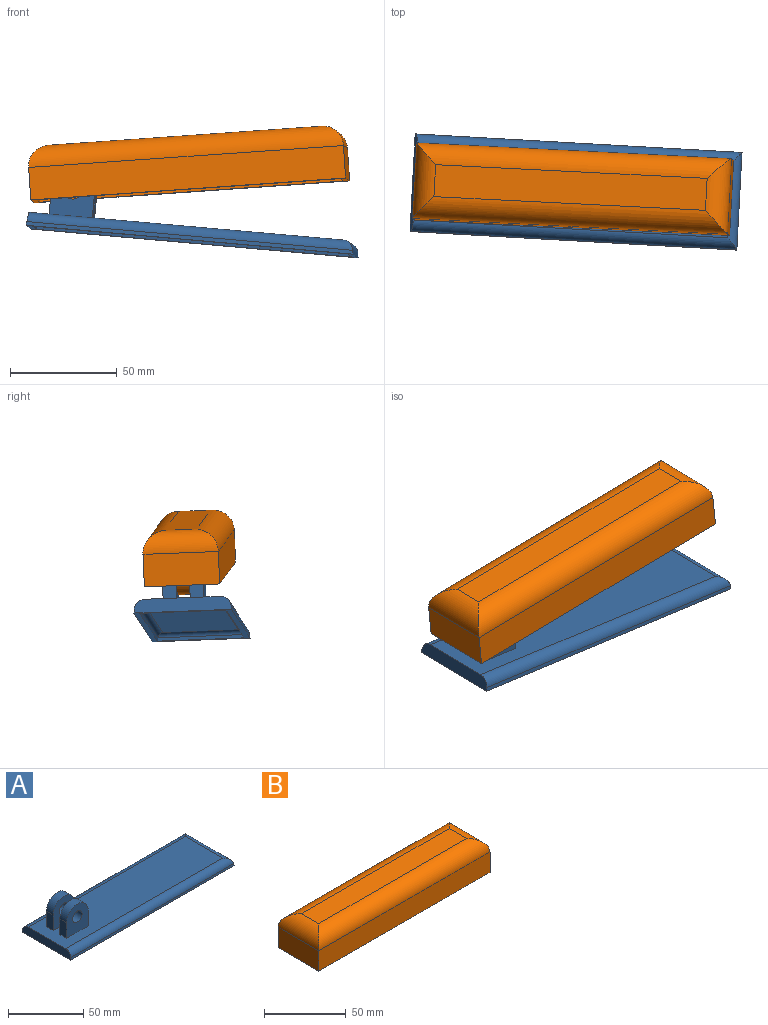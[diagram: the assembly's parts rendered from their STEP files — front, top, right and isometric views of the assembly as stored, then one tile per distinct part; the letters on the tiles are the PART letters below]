
ASSEMBLY  parts=2 mates=1
PART A: 41 faces, bbox 153.7x45.8x29.2 mm
  f0: plane 12.7x6.35mm, normal (1,0,0), area 80.6mm2, adj f1,f4,f5,f6
  f1: cylinder r=10.16mm len=20.32mm, axis (0,-1,0), area 202.7mm2, adj f0,f3,f4,f5
  f2: cylinder r=4.45mm len=8.89mm, axis (0,-1,0), area 177.3mm2, adj f4,f5
  f3: plane 12.7x6.35mm, normal (-1,0,0), area 80.6mm2, adj f1,f4,f5,f6
  f4: plane 22.86x20.32mm, normal (0,-1,0), area 358.1mm2, adj f0,f1,f2,f3,f6
  f5: plane 22.86x20.32mm, normal (0,1,0), area 358.1mm2, adj f0,f1,f2,f3,f6
  f6: plane 147.83x35.3mm, normal (0,0,1), area 4960.5mm2, adj f0,f3,f4,f5,f7,f10,f11,f12
  f7: plane 12.7x6.35mm, normal (1,0,0), area 80.6mm2, adj f6,f8,f11,f12
  f8: cylinder r=10.16mm len=20.32mm, axis (0,-1,0), area 202.7mm2, adj f7,f10,f11,f12
  f9: cylinder r=4.45mm len=8.89mm, axis (0,-1,0), area 177.3mm2, adj f11,f12
  f10: plane 12.7x6.35mm, normal (-1,0,0), area 80.6mm2, adj f6,f8,f11,f12
  f11: plane 22.86x20.32mm, normal (0,-1,0), area 358.1mm2, adj f6,f7,f8,f9,f10
  f12: plane 22.86x20.32mm, normal (0,1,0), area 358.1mm2, adj f6,f7,f8,f9,f10
  f13: plane 45.79x1.8mm, normal (0.99,0,0.1), area 82.6mm2, adj f14,f16,f17,f19
  f14: plane 153.74x1.8mm, normal (0,0.99,0.1), area 278.1mm2, adj f13,f15,f17,f20
  f15: plane 45.79x6.35mm, normal (-0.99,0,0.1), area 279.4mm2, adj f6,f14,f16,f17,f18,f20
  f16: plane 153.74x1.8mm, normal (0,-0.99,0.1), area 278.1mm2, adj f13,f15,f17,f18
  f17: plane 153.74x45.79mm, normal (0,0,-1), area 993.1mm2, adj f13,f14,f15,f16,f34,f35,f36,f37
  f18: cylinder r=5.08mm len=153.36mm, axis (1,0,0), area 1125.3mm2, adj f6,f15,f16,f19
  f19: cylinder r=5.08mm len=45.41mm, axis (0,-1,0), area 309.1mm2, adj f6,f13,f18,f20
  f20: cylinder r=5.08mm len=153.36mm, axis (1,0,0), area 1125.3mm2, adj f6,f14,f15,f19
  f21: plane 15.24x1.27mm, normal (-1,0,0), area 19.4mm2, adj f22,f25,f26,f27
  f22: cylinder r=7.62mm len=15.24mm, axis (0,-1,0), area 30.4mm2, adj f21,f24,f25,f26
  f23: cylinder r=6.99mm len=13.97mm, axis (0,-1,0), area 55.7mm2, adj f25,f26
  f24: plane 15.24x1.27mm, normal (1,0,0), area 19.4mm2, adj f22,f25,f26,f27
  f25: plane 22.86x15.24mm, normal (0,1,0), area 170.2mm2, adj f21,f22,f23,f24,f27
  f26: plane 22.86x15.24mm, normal (0,-1,0), area 170.2mm2, adj f21,f22,f23,f24,f27
  f27: plane 145.54x35.3mm, normal (0,0,-1), area 5099.1mm2, adj f21,f24,f25,f26,f28,f31,f32,f33
  f28: plane 15.24x1.27mm, normal (-1,0,0), area 19.4mm2, adj f27,f29,f32,f33
  f29: cylinder r=7.62mm len=15.24mm, axis (0,-1,0), area 30.4mm2, adj f28,f31,f32,f33
  f30: cylinder r=6.99mm len=13.97mm, axis (0,-1,0), area 55.7mm2, adj f32,f33
  f31: plane 15.24x1.27mm, normal (1,0,0), area 19.4mm2, adj f27,f29,f32,f33
  f32: plane 22.86x15.24mm, normal (0,1,0), area 170.2mm2, adj f27,f28,f29,f30,f31
  f33: plane 22.86x15.24mm, normal (0,-1,0), area 170.2mm2, adj f27,f28,f29,f30,f31
  f34: plane 40.68x1.54mm, normal (-0.99,0,-0.1), area 62.6mm2, adj f17,f35,f37,f39
  f35: plane 148.63x1.54mm, normal (0,-0.99,-0.1), area 229.2mm2, adj f17,f34,f36,f40
  f36: plane 40.68x3.81mm, normal (0.99,0,-0.1), area 152.1mm2, adj f17,f27,f35,f37,f38,f40
  f37: plane 148.63x1.54mm, normal (0,0.99,-0.1), area 229.2mm2, adj f17,f34,f36,f38
  f38: cylinder r=2.54mm len=148.3mm, axis (1,0,0), area 548.1mm2, adj f27,f36,f37,f39
  f39: cylinder r=2.54mm len=40.35mm, axis (0,-1,0), area 143mm2, adj f27,f34,f38,f40
  f40: cylinder r=2.54mm len=148.3mm, axis (1,0,0), area 548.1mm2, adj f27,f35,f36,f39
PART B: 25 faces, bbox 147.8x35.3x31.1 mm
  f0: plane 28.58x19.05mm, normal (0,1,0), area 443.3mm2, adj f16,f21,f22,f23,f24
  f1: plane 28.58x19.05mm, normal (0,-1,0), area 443.3mm2, adj f16,f21,f22,f23,f24
  f2: plane 35.3x15.24mm, normal (1,0,0), area 538mm2, adj f3,f5,f7,f10
  f3: plane 147.83x15.24mm, normal (0,1,0), area 2252.9mm2, adj f2,f4,f7,f11
  f4: plane 35.3x15.24mm, normal (-1,0,0), area 538mm2, adj f3,f5,f7,f9
  f5: plane 147.83x15.24mm, normal (0,-1,0), area 2252.9mm2, adj f2,f4,f7,f8
  f6: plane 127.51x14.98mm, normal (0,0,1), area 1910.3mm2, adj f8,f9,f10,f11
  f7: plane 147.83x35.3mm, normal (0,0,-1), area 904.5mm2, adj f2,f3,f4,f5,f12,f13,f14,f15
  f8: cylinder r=10.16mm len=147.83mm, axis (1,0,0), area 2241.4mm2, adj f5,f6,f9,f10
  f9: cylinder r=10.16mm len=35.3mm, axis (0,-1,0), area 445.6mm2, adj f4,f6,f8,f11
  f10: cylinder r=10.16mm len=35.3mm, axis (0,1,0), area 445.6mm2, adj f2,f6,f8,f11
  f11: cylinder r=10.16mm len=147.83mm, axis (-1,0,0), area 2241.4mm2, adj f3,f6,f9,f10
  f12: plane 30.22x15.24mm, normal (-1,0,0), area 460.6mm2, adj f7,f13,f15,f19
  f13: plane 142.75x15.24mm, normal (0,-1,0), area 2175.4mm2, adj f7,f12,f14,f20
  f14: plane 30.22x15.24mm, normal (1,0,0), area 460.6mm2, adj f7,f13,f15,f18
  f15: plane 142.75x15.24mm, normal (0,1,0), area 2175.4mm2, adj f7,f12,f14,f17
  f16: plane 127.51x14.98mm, normal (0,0,-1), area 1789.3mm2, adj f0,f1,f17,f18,f19,f20,f22
  f17: cylinder r=7.62mm len=142.75mm, axis (1,0,0), area 1642.3mm2, adj f15,f16,f18,f19
  f18: cylinder r=7.62mm len=30.22mm, axis (0,-1,0), area 295.5mm2, adj f14,f16,f17,f20,f21
  f19: cylinder r=7.62mm len=30.22mm, axis (0,1,0), area 295.5mm2, adj f12,f16,f17,f20
  f20: cylinder r=7.62mm len=142.75mm, axis (-1,0,0), area 1642.3mm2, adj f13,f16,f18,f19
  f21: plane 19.05x6.35mm, normal (-1,0,0), area 121mm2, adj f0,f1,f18,f24
  f22: plane 19.05x6.35mm, normal (1,0,0), area 121mm2, adj f0,f1,f16,f24
  f23: cylinder r=4.45mm len=8.89mm, axis (0,1,0), area 177.3mm2, adj f0,f1
  f24: cylinder r=9.53mm len=19.05mm, axis (0,1,0), area 190mm2, adj f0,f1,f21,f22
PLACE A rot(axis=(-0.33,0.81,-0.5),6.3deg) t=(-76.16,48.75,83.4)mm fixed
PLACE B rot(axis=(-0.42,-0.72,-0.55),5.4deg) t=(-79.25,-34.56,105.18)mm
MATE revolute B.f23 <-> A.f1  axis (0.05,1,-0.04) through (-96.16,53.04,104.19)mm
